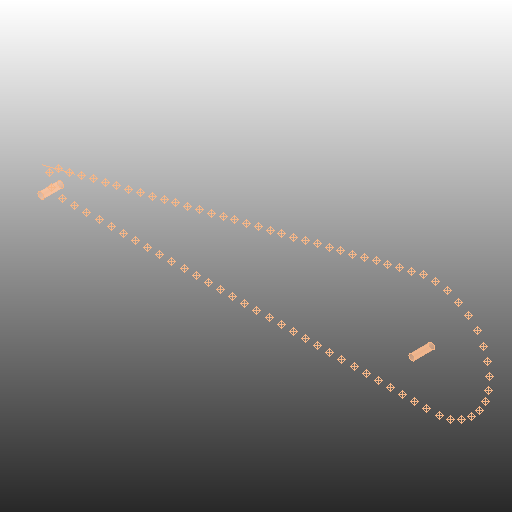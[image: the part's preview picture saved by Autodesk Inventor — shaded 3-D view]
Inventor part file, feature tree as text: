
AUTODESK INVENTOR PART (.ipt)
format: ipt  version: 2021 (Build 250183000, 183)  size: 123,392 bytes
history: native  units: in
note: dims shown in document units (in); Inventor stores cm internally (conversion verified against a paired STEP export)
features: other x83, sketch x3, extrude x2, pattern_linear x1
ambient origin geometry x8: Origin, YZ Plane, XZ Plane, XY Plane, X Axis, Y Axis, Z Axis, Center Point
bodies: Body1 (feature_tree), Body2 (feature_tree)
feature tree (89):
  sketch  "Sketch1"  dims[d3=31.6185in]
  other  "Work Point1"
  pattern_linear  "Rectangular Pattern1"  Spacing1=1.1156in  [1 undecoded]
  other  "Work Axis1"
  other  "Work Point2"
  other  "Work Point3"
  other  "Work Point4"
  other  "Work Point5"
  other  "Work Point6"
  other  "Work Point7"
  other  "Work Point8"
  other  "Work Point9"
  other  "Work Point10"
  other  "Work Point50"
  other  "Work Point51"
  other  "Work Point52"
  other  "Work Point53"
  other  "Work Point54"
  other  "Work Point55"
  other  "Work Point56"
  other  "Work Point57"
  other  "Work Point58"
  other  "Work Point59"
  other  "Work Point60"
  other  "Work Point61"
  other  "Work Point62"
  other  "Work Point63"
  other  "Work Point64"
  other  "Work Point65"
  other  "Work Point66"
  other  "Work Point67"
  other  "Work Point68"
  other  "Work Point69"
  other  "Work Point70"
  other  "Work Point71"
  other  "Work Point72"
  other  "Work Point73"
  other  "Work Point74"
  other  "Work Point75"
  other  "Work Point76"
  other  "Work Point77"
  other  "Work Point78"
  other  "Work Point79"
  other  "Work Point80"
  other  "Work Point81"
  other  "Work Point82"
  other  "Work Point83"
  sketch  "Sketch2"  dims[d5=11.9109in]
  other  "Srf1"
  sketch  "Sketch3"  dims[d6=11.9109in d7=1.1156in d8=6.2463in d9=0.2in d10=0.625in d11=0.0in d12=0.2in d13=0.625in d14=0.0in]
  other  "Srf2"
  other  "Work Point97"
  other  "Work Point98"
  other  "Work Point99"
  other  "Work Point100"
  other  "Work Point101"
  other  "Work Point102"
  other  "Work Point103"
  other  "Work Point104"
  other  "Work Point105"
  other  "Work Point106"
  other  "Work Point107"
  other  "Work Point108"
  other  "Work Point109"
  other  "Work Point110"
  other  "Work Point111"
  other  "Work Point112"
  other  "Work Point113"
  other  "Work Point114"
  other  "Work Point123"
  other  "Work Point124"
  other  "Work Point125"
  other  "Work Point126"
  other  "Work Point127"
  other  "Work Point128"
  other  "Work Point129"
  other  "Work Point130"
  other  "Work Point131"
  other  "Work Point132"
  other  "Work Point133"
  other  "Work Point134"
  other  "Work Point135"
  other  "Work Point136"
  other  "Work Point137"
  other  "Work Point138"
  other  "Work Point139"
  other  "Work Point140"
  extrude  "ExtrusionSrf1"  Depth=6.2463in
  extrude  "ExtrusionSrf2"  Depth=0.2in
note: 1 required parameter value undecoded (feature->parameter linkage not recoverable at this tier; creation-order binding heuristic only, values carry confidence <= 0.55)
